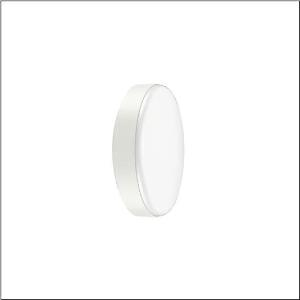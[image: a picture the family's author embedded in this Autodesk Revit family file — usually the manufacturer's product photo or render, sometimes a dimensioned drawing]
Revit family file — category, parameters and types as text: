
# Revit family: rondel_31_51wc10da32as
name_source: partatom
category: Lighting Fixtures
units: mm (PartAtom-declared; Revit-internal decimal feet)

## family parameters
Cut with Voids When Loaded = No
Host = Face
Light Source = No
Part Type = Normal
Room Calculation Point = No
Round Connector Dimension = Use Diameter
Shared = No

## types (1)
- Rondel 31 (1 x LED, 2450 lm, 20.4 W, 3000K)
    Apparent Load = 20 VA
    CIE Flux Codes = 44 75 94 94 100
    Color Rendering = 80
    Color Temperature = 3000K
    Default Elevation = 1800 mm
    Description = Rondel 31, wall and ceiling luminaire, primary optical cover: cover, of PC, opal, light emission: direct distribution, primary light characteristic: symmetric, installation type: surface-mounted, LED, rated luminous flux: 2.450lm, luminous efficacy: 120lm/W, light colour: 830, colour temperature: 3000K, with terminal, 5-pole, max. 2.5mm², mains connection: 220..240V, AC, 50/60Hz, rated input power: 20.5W, luminaire housing, of PC, traffic white (RAL 9016), diameter: 350mm, brightness and presence sensor, HF sensor, protection rating (complete): IP65, insulation class (complete): insulation class II (safety insulation), certification: CE, impact resistance: IK10, permissible operating ambient temperature: -20..+40°C, permissible storage temperature: -20..+60°C, packaging unit: 1 piece
    Height = 97 mm
    Lamp = 1 x LED
    Lamp Light Flux = 2450 lm
    Lamp Power = 20.4 W
    Lamp count = 1
    Length = 350 mm
    Luminous efficacy = 120 lm/W
    Manufacturer = Siteco
    ModVariant = No
    Model = 51WC10DA32AS
    Mounting Place = Ceiling
    Mounting Type = Surface mounted
    Number of Poles = 1
    OnlyDefault = Yes
    Power Factor = 1
    Product Name = Rondel 31
    Product group = wall and ceiling luminaire
    ProductGroupID = 301
    Protection Class = Protection class II
    Protection Degree = IP 65
    RLX_Detail_Level = 1
    RLX_Emergency_Light_Flux = 0 lm
    RLX_Emergency_Type = 0
    RLX_Emergency_Type_DB = No
    RlxData = <blob elided: 29765 chars, md5=e5d57eab>
    Socket = socket
    Standby Power = 0 W
    System Light Flux = 2450 lm
    System Power = 20 W
    Type Comments = Product without accessories
    Type Image = l_1007027.jpg
    URL = http://relux.com
    VarID = ---
    Voltage = 0 V
    Weight = 0.00 kg
    Width = 0 mm  [stored 0 ft]

note: [stored X ft] marks values corroborated as IEEE doubles in the binary element streams (Revit-internal decimal feet)

## geometry (parser evidence)
native form markers: Blend x4, Sweep x13
no freeform markers — native parametric forms only
